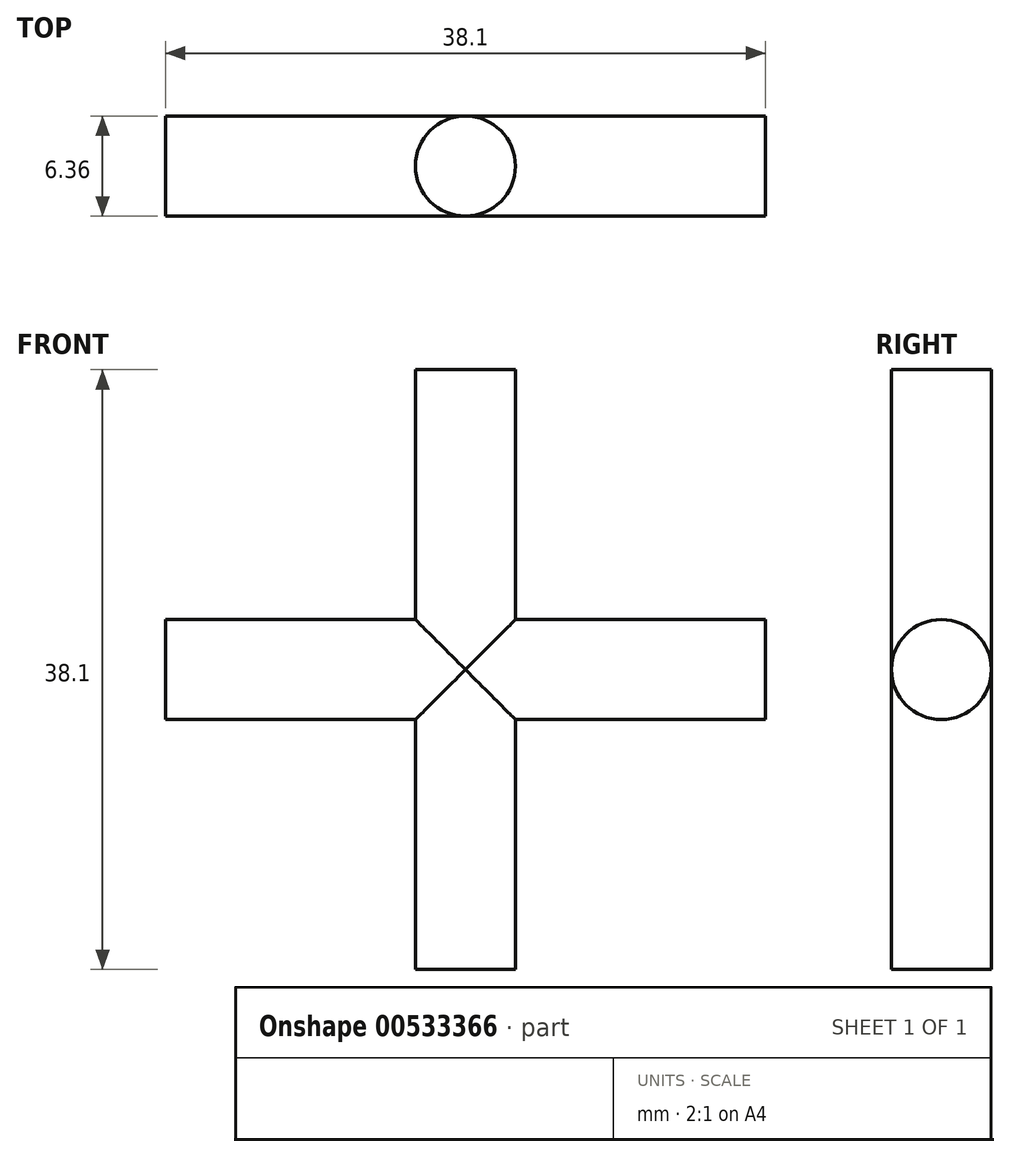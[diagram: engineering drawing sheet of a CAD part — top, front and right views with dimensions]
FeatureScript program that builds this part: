
annotation { "Feature Type Name" : "Feature", "Feature Type Description" : "" }
export const myFeature = defineFeature(function(context is Context, id is Id, definition is map)
    precondition{}
    {
        {
            var Q0;
            Q0=qCreatedBy(makeId("Top.planeOp"),FACE);
            var sketch = newSketch(context, id + "F0", { "sketchPlane" : qUnion([Q0])});
            skCircle(sketch, "E0", {"center": v(0, 0) * mm, "radius": 3.18 * mm});
            skSolve(sketch);
        }
        {
            var Q0;
            Q0 = qSketchRegion(id + "F0", true);
            extrude(context, id + "F1", {"entities" : qUnion([Q0]), "endBound" : BoundingType.SYMMETRIC, "depth" : 38.1 * mm, "offsetDistance" : 25.4 * mm});
        }
        {
            var Q0;
            Q0=qCreatedBy(makeId("Right.planeOp"),FACE);
            var sketch = newSketch(context, id + "F2", { "sketchPlane" : qUnion([Q0])});
            skCircle(sketch, "E1", {"center": v(0, 0) * mm, "radius": 3.18 * mm});
            skSolve(sketch);
        }
        {
            var Q0;
            Q0 = qSketchRegion(id + "F2", true);
            extrude(context, id + "F3", {"entities" : qUnion([Q0]), "operationType" : NewBodyOperationType.ADD, "endBound" : BoundingType.SYMMETRIC, "depth" : 38.1 * mm, "offsetDistance" : 25.4 * mm});
        }
    });
